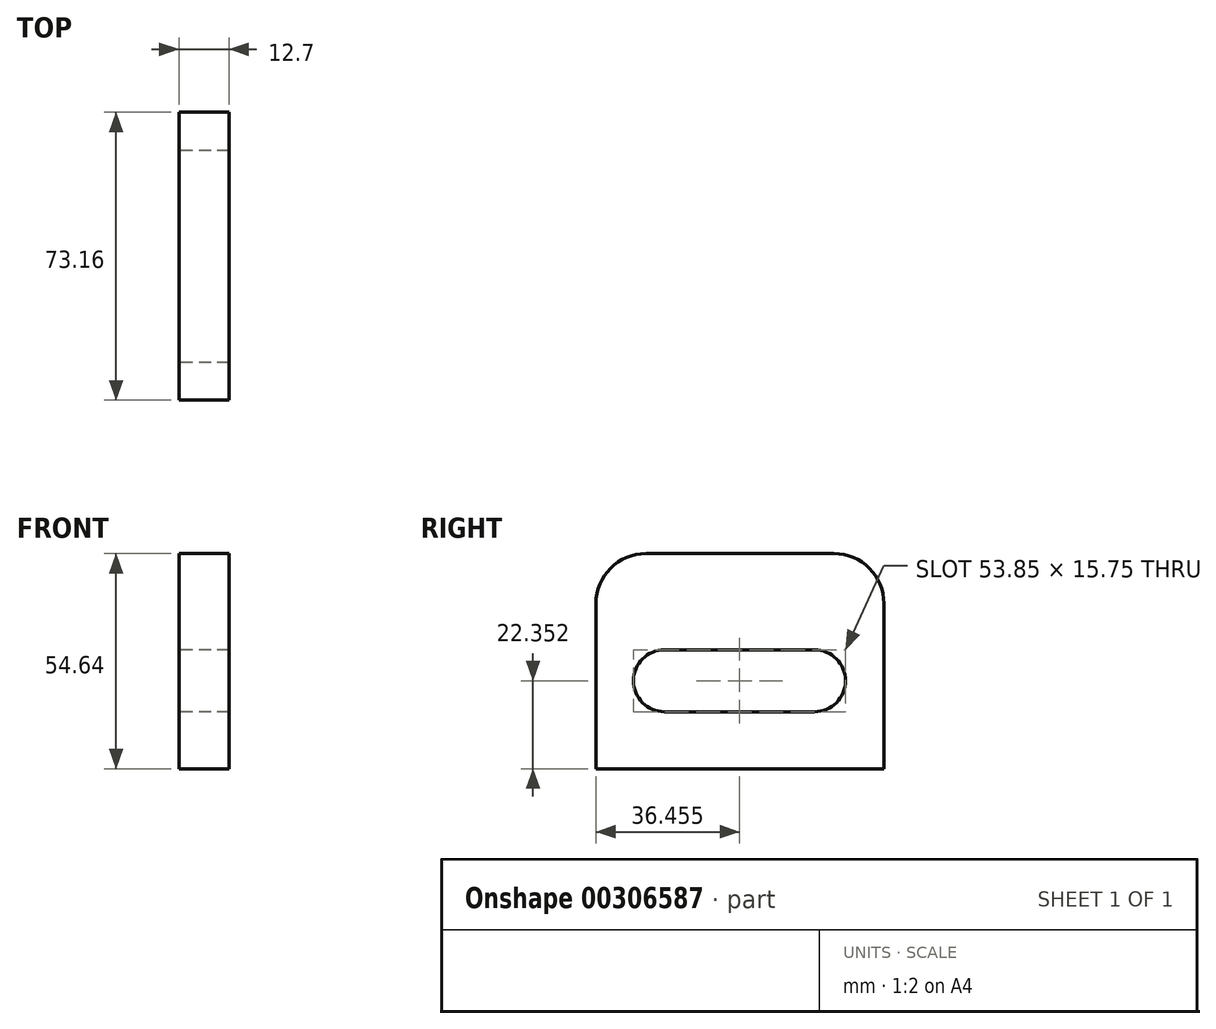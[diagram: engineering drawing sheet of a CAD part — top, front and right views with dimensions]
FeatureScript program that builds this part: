
annotation { "Feature Type Name" : "Feature", "Feature Type Description" : "" }
export const myFeature = defineFeature(function(context is Context, id is Id, definition is map)
    precondition{}
    {
        {
            var Q0;
            Q0=qCreatedBy(makeId("Right.planeOp"),FACE);
            var sketch = newSketch(context, id + "F0", { "sketchPlane" : qUnion([Q0])});
            skLineSegment(sketch, "E0.bottom", {"start": v(0, 0) * mm, "end": v(73.16, 0) * mm});
            skLineSegment(sketch, "E0.top", {"start": v(12.7, 54.64) * mm, "end": v(60.46, 54.64) * mm});
            skLineSegment(sketch, "E0.left", {"start": v(0, 0) * mm, "end": v(0, 41.94) * mm});
            skLineSegment(sketch, "E0.right", {"start": v(73.16, 0) * mm, "end": v(73.16, 41.94) * mm});
            skLineSegment(sketch, "E1.bottom", {"start": v(17.4, 30.23) * mm, "end": v(55.5, 30.23) * mm});
            skLineSegment(sketch, "E1.top", {"start": v(17.4, 14.48) * mm, "end": v(55.5, 14.48) * mm});
            skLineSegment(sketch, "E1.left", {"start": v(9.53, 22.35) * mm, "end": v(9.53, 22.35) * mm});
            skLineSegment(sketch, "E1.right", {"start": v(63.38, 22.35) * mm, "end": v(63.38, 22.35) * mm});
            skPoint(sketch, "E2.visualSharp", {"position": v(9.53, 30.23) * mm});
            skArc(sketch, "E2.filletArc", {"start": v(17.4, 30.23) * mm, "mid": v(11.84, 27.92) * mm, "end": v(9.53, 22.35) * mm});
            skPoint(sketch, "E3.visualSharp", {"position": v(63.38, 30.23) * mm});
            skArc(sketch, "E3.filletArc", {"start": v(63.38, 22.35) * mm, "mid": v(61.07, 27.92) * mm, "end": v(55.5, 30.23) * mm});
            skPoint(sketch, "E4.visualSharp", {"position": v(63.38, 14.48) * mm});
            skArc(sketch, "E4.filletArc", {"start": v(55.5, 14.48) * mm, "mid": v(61.07, 16.78) * mm, "end": v(63.38, 22.35) * mm});
            skPoint(sketch, "E5.visualSharp", {"position": v(9.53, 14.48) * mm});
            skArc(sketch, "E5.filletArc", {"start": v(9.53, 22.35) * mm, "mid": v(11.84, 16.78) * mm, "end": v(17.4, 14.48) * mm});
            skPoint(sketch, "E6.visualSharp", {"position": v(0, 54.64) * mm});
            skArc(sketch, "E6.filletArc", {"start": v(12.7, 54.64) * mm, "mid": v(3.72, 50.92) * mm, "end": v(0, 41.94) * mm});
            skPoint(sketch, "E7.visualSharp", {"position": v(73.16, 54.64) * mm});
            skArc(sketch, "E7.filletArc", {"start": v(73.16, 41.94) * mm, "mid": v(69.44, 50.92) * mm, "end": v(60.46, 54.64) * mm});
            skSolve(sketch);
        }
        {
            var Q0;
            Q0 = qSketchRegion(id + "F0", true);
            extrude(context, id + "F1", {"entities" : qUnion([Q0]), "depth" : 12.7 * mm});
        }
    });
